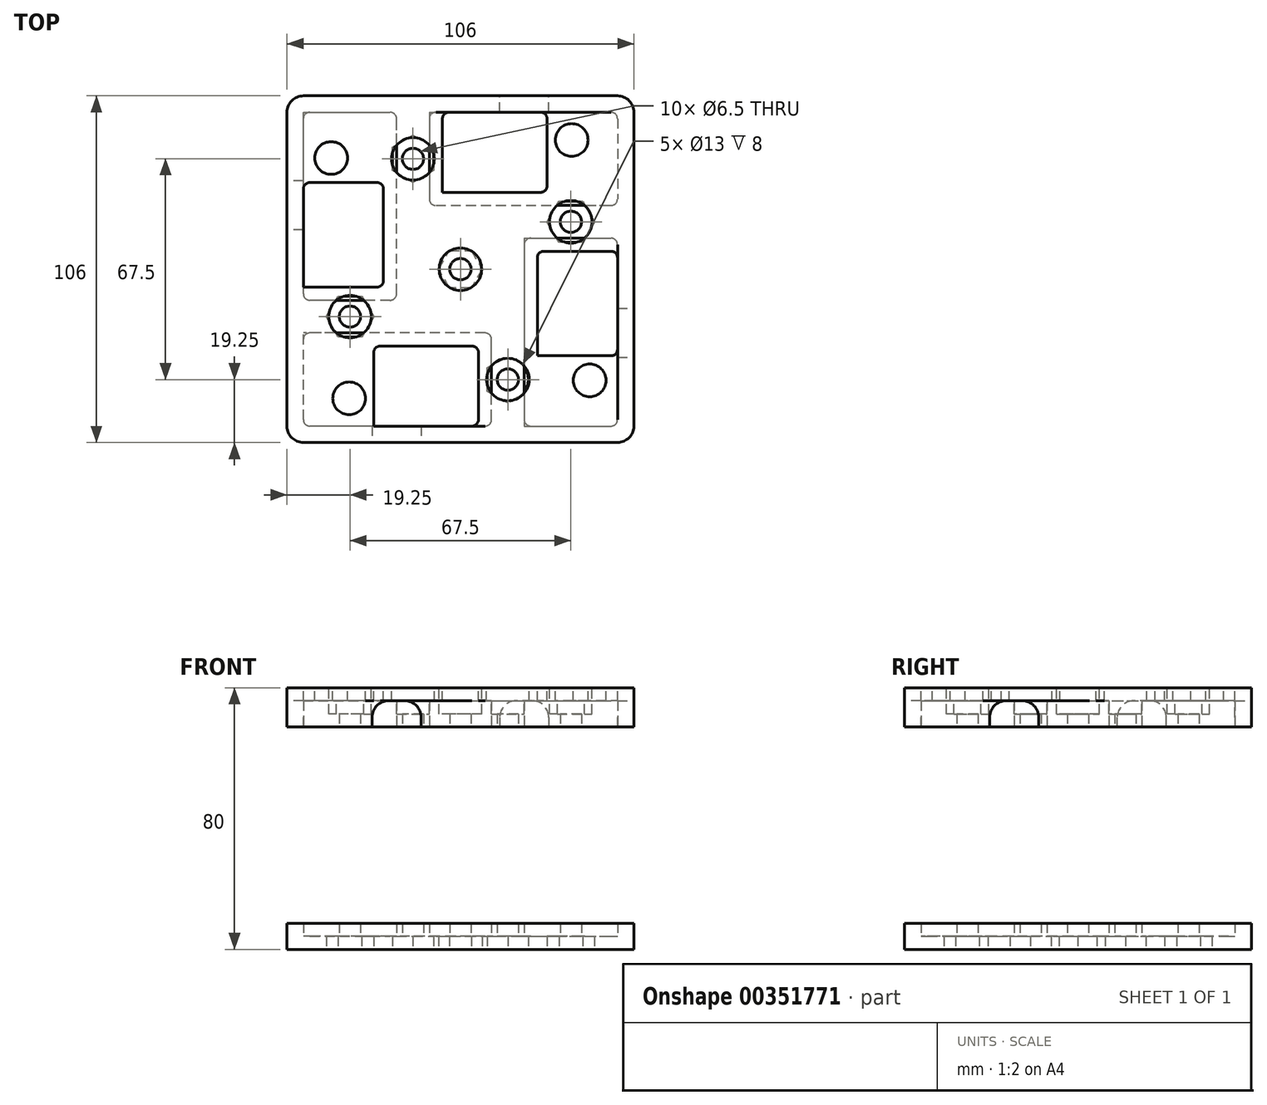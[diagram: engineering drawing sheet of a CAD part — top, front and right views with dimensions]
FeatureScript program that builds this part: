
annotation { "Feature Type Name" : "Feature", "Feature Type Description" : "" }
export const myFeature = defineFeature(function(context is Context, id is Id, definition is map)
    precondition{}
    {
        {
            var Q0;
            Q0=qCreatedBy(makeId("Top.planeOp"),FACE);
            var sketch = newSketch(context, id + "F0", { "sketchPlane" : qUnion([Q0])});
            skPoint(sketch, "E0.middle", {"position": v(0, 0) * mm});
            skCircle(sketch, "E1", {"center": v(0, 0) * mm, "radius": 3.25 * mm});
            skLineSegment(sketch, "E2.bottom", {"start": v(14.5, 14.5) * mm, "end": v(53, 14.5) * mm});
            skLineSegment(sketch, "E2.top", {"start": v(14.5, -53) * mm, "end": v(53, -53) * mm});
            skLineSegment(sketch, "E2.left", {"start": v(14.5, 14.5) * mm, "end": v(14.5, -53) * mm});
            skLineSegment(sketch, "E2.right", {"start": v(53, 14.5) * mm, "end": v(53, -53) * mm});
            skLineSegment(sketch, "E3.0", {"start": v(19.5, 9.5) * mm, "end": v(48, 9.5) * mm});
            skLineSegment(sketch, "E3.1", {"start": v(19.5, 9.5) * mm, "end": v(19.5, -48) * mm});
            skLineSegment(sketch, "E3.2", {"start": v(19.5, -48) * mm, "end": v(48, -48) * mm});
            skLineSegment(sketch, "E3.3", {"start": v(48, 9.5) * mm, "end": v(48, -48) * mm});
            skLineSegment(sketch, "E4.bottom", {"start": v(14.5, -53) * mm, "end": v(-53, -53) * mm});
            skLineSegment(sketch, "E4.top", {"start": v(14.5, -14.5) * mm, "end": v(-53, -14.5) * mm});
            skLineSegment(sketch, "E4.left", {"start": v(14.5, -53) * mm, "end": v(14.5, -14.5) * mm});
            skLineSegment(sketch, "E4.right", {"start": v(-53, -53) * mm, "end": v(-53, -14.5) * mm});
            skLineSegment(sketch, "E5.bottom", {"start": v(-53, -14.5) * mm, "end": v(-14.5, -14.5) * mm});
            skLineSegment(sketch, "E5.top", {"start": v(-53, 53) * mm, "end": v(-14.5, 53) * mm});
            skLineSegment(sketch, "E5.left", {"start": v(-53, -14.5) * mm, "end": v(-53, 53) * mm});
            skLineSegment(sketch, "E6.bottom", {"start": v(-14.5, 53) * mm, "end": v(53, 53) * mm});
            skLineSegment(sketch, "E6.right", {"start": v(53, 53) * mm, "end": v(53, 14.5) * mm});
            skLineSegment(sketch, "E7.0", {"start": v(-9.5, 19.5) * mm, "end": v(48, 19.5) * mm});
            skLineSegment(sketch, "E7.1", {"start": v(48, 48) * mm, "end": v(48, 19.5) * mm});
            skLineSegment(sketch, "E7.2", {"start": v(-9.5, 48) * mm, "end": v(48, 48) * mm});
            skLineSegment(sketch, "E8.0", {"start": v(-19.5, -9.5) * mm, "end": v(-19.5, 48) * mm});
            skLineSegment(sketch, "E8.1", {"start": v(-48, 48) * mm, "end": v(-19.5, 48) * mm});
            skLineSegment(sketch, "E9", {"start": v(-9.5, 48) * mm, "end": v(-9.5, 19.5) * mm});
            skLineSegment(sketch, "E10", {"start": v(-19.5, -9.5) * mm, "end": v(-48, -9.5) * mm});
            skLineSegment(sketch, "E11.trimOffspring", {"start": v(-48, -9.5) * mm, "end": v(-48, 48) * mm});
            skLineSegment(sketch, "E12.0", {"start": v(9.5, -19.5) * mm, "end": v(-48, -19.5) * mm});
            skLineSegment(sketch, "E12.1", {"start": v(9.5, -48) * mm, "end": v(9.5, -19.5) * mm});
            skLineSegment(sketch, "E12.2", {"start": v(9.5, -48) * mm, "end": v(-48, -48) * mm});
            skLineSegment(sketch, "E12.3", {"start": v(-48, -48) * mm, "end": v(-48, -19.5) * mm});
            skLineSegment(sketch, "E13", {"start": v(-14.5, 53) * mm, "end": v(-14.5, -14.5) * mm});
            skLineSegment(sketch, "E14", {"start": v(14.5, 14.5) * mm, "end": v(-14.5, 14.5) * mm});
            skCircle(sketch, "E15", {"center": v(14.5, -33.75) * mm, "radius": 3.25 * mm});
            skCircle(sketch, "E16", {"center": v(-33.75, -14.5) * mm, "radius": 3.25 * mm});
            skCircle(sketch, "E17", {"center": v(33.75, 14.5) * mm, "radius": 3.25 * mm});
            skCircle(sketch, "E18", {"center": v(-14.5, 33.75) * mm, "radius": 3.25 * mm});
            skPoint(sketch, "E19.0.midPoint", {"position": v(20.3, -33.75) * mm});
            skLineSegment(sketch, "E20.1.3", {"start": v(30.22, 19.5) * mm, "end": v(30.4, 19.81) * mm});
            skSolve(sketch);
        }
        {
            var Q0;
            Q0 = qSketchRegion(id + "F0", true);
            var Q1;
            Q1=makeQuery(id+"F0.imprint","IMPRINT",FACE,{"disambiguationData":[TD([[makeQuery(id+"F0.imprint","IMPRINT",EDGE,{"derivedFrom":sQuery(id+"F0.wireOp",EDGE,"E1")}),-1.0]])]});
            extrude(context, id + "F1", {"entities" : qUnion([Q0, Q1]), "depth" : 8 * mm, "offsetDistance" : 25 * mm});
        }
        {
            var Q0;
            Q0 = qSketchRegion(id + "F0", true);
            var Q1;
            Q1=makeQuery(id+"F0.imprint","IMPRINT",FACE,{"disambiguationData":[TD([[makeQuery(id+"F0.imprint","IMPRINT",EDGE,{"derivedFrom":sQuery(id+"F0.wireOp",EDGE,"E12.0")}),1.0]])]});
            var Q2;
            Q2=makeQuery(id+"F0.imprint","IMPRINT",FACE,{"disambiguationData":[TD([[makeQuery(id+"F0.imprint","IMPRINT",EDGE,{"derivedFrom":sQuery(id+"F0.wireOp",EDGE,"E8.0")}),1.0]])]});
            var Q3;
            {var subQ0=sQuery(id+"F0.wireOp",EDGE,"E7.1");Q3=makeQuery(id+"F0.imprint","IMPRINT",FACE,{"disambiguationData":[TD([[makeQuery(id+"F0.imprint","IMPRINT",EDGE,{"derivedFrom":subQ0}),-1.0]])]});}
            var Q4;
            Q4=makeQuery(id+"F0.imprint","IMPRINT",FACE,{"disambiguationData":[TD([[makeQuery(id+"F0.imprint","IMPRINT",EDGE,{"derivedFrom":sQuery(id+"F0.wireOp",EDGE,"E3.0")}),-1.0]])]});
            var Q5;
            Q5=makeQuery(id+"F0.imprint","IMPRINT",FACE,{"disambiguationData":[TD([[makeQuery(id+"F0.imprint","IMPRINT",EDGE,{"derivedFrom":sQuery(id+"F0.wireOp",EDGE,"E1")}),-1.0]])]});
            extrude(context, id + "F2", {"entities" : qUnion([Q0, Q1, Q2, Q3, Q4, Q5]), "operationType" : NewBodyOperationType.ADD, "depth" : 4 * mm, "offsetDistance" : 25 * mm});
        }
        {
            var Q0;
            Q0 = qSketchRegion(id + "F0", true);
            var Q1;
            Q1=makeQuery(id+"F0.imprint","IMPRINT",FACE,{"disambiguationData":[TD([[makeQuery(id+"F0.imprint","IMPRINT",EDGE,{"derivedFrom":sQuery(id+"F0.wireOp",EDGE,"E1")}),-1.0]])]});
            extrude(context, id + "F3", {"entities" : qUnion([Q0, Q1]), "depth" : 80 * mm, "offsetDistance" : 25 * mm, "hasSecondDirection" : true, "secondDirectionOppositeDirection" : false, "secondDirectionDepth" : 68 * mm});
        }
        {
            var Q0;
            Q0 = qSketchRegion(id + "F0", true);
            var Q1;
            Q1=makeQuery(id+"F2.boolean.opBoolean","SPLIT",FACE,{"disambiguationData":[TD([makeQuery(id+"F1.opExtrude","SWEPT_FACE",FACE,{"disambiguationData":[OSD([sQuery(id+"F0.wireOp",EDGE,"E8.0")])]})])],"derivedFrom":makeQuery(id+"F2.opExtrude","CAP_FACE",FACE,{"disambiguationData":[OSD([sQuery(id+"F0.wireOp",EDGE,"E1"),sQuery(id+"F0.wireOp",EDGE,"E2.top"),sQuery(id+"F0.wireOp",EDGE,"E2.right"),sQuery(id+"F0.wireOp",EDGE,"E4.bottom"),sQuery(id+"F0.wireOp",EDGE,"E4.right"),sQuery(id+"F0.wireOp",EDGE,"E5.top"),sQuery(id+"F0.wireOp",EDGE,"E5.left"),sQuery(id+"F0.wireOp",EDGE,"E6.bottom"),sQuery(id+"F0.wireOp",EDGE,"E6.right")])],"isStart":false})});
            var Q2;
            Q2=makeQuery(id+"F2.boolean.opBoolean","SPLIT",FACE,{"disambiguationData":[TD([makeQuery(id+"F1.opExtrude","SWEPT_FACE",FACE,{"disambiguationData":[OSD([sQuery(id+"F0.wireOp",EDGE,"E7.0")])]})])],"derivedFrom":makeQuery(id+"F2.opExtrude","CAP_FACE",FACE,{"disambiguationData":[OSD([sQuery(id+"F0.wireOp",EDGE,"E1"),sQuery(id+"F0.wireOp",EDGE,"E2.top"),sQuery(id+"F0.wireOp",EDGE,"E2.right"),sQuery(id+"F0.wireOp",EDGE,"E4.bottom"),sQuery(id+"F0.wireOp",EDGE,"E4.right"),sQuery(id+"F0.wireOp",EDGE,"E5.top"),sQuery(id+"F0.wireOp",EDGE,"E5.left"),sQuery(id+"F0.wireOp",EDGE,"E6.bottom"),sQuery(id+"F0.wireOp",EDGE,"E6.right")])],"isStart":false})});
            var Q3;
            Q3=makeQuery(id+"F2.boolean.opBoolean","SPLIT",FACE,{"disambiguationData":[TD([makeQuery(id+"F1.opExtrude","SWEPT_FACE",FACE,{"disambiguationData":[OSD([sQuery(id+"F0.wireOp",EDGE,"E3.0")])]})])],"derivedFrom":makeQuery(id+"F2.opExtrude","CAP_FACE",FACE,{"disambiguationData":[OSD([sQuery(id+"F0.wireOp",EDGE,"E1"),sQuery(id+"F0.wireOp",EDGE,"E2.top"),sQuery(id+"F0.wireOp",EDGE,"E2.right"),sQuery(id+"F0.wireOp",EDGE,"E4.bottom"),sQuery(id+"F0.wireOp",EDGE,"E4.right"),sQuery(id+"F0.wireOp",EDGE,"E5.top"),sQuery(id+"F0.wireOp",EDGE,"E5.left"),sQuery(id+"F0.wireOp",EDGE,"E6.bottom"),sQuery(id+"F0.wireOp",EDGE,"E6.right")])],"isStart":false})});
            var Q4;
            Q4=makeQuery(id+"F2.boolean.opBoolean","SPLIT",FACE,{"disambiguationData":[TD([makeQuery(id+"F1.opExtrude","SWEPT_FACE",FACE,{"disambiguationData":[OSD([sQuery(id+"F0.wireOp",EDGE,"E12.0")])]})])],"derivedFrom":makeQuery(id+"F2.opExtrude","CAP_FACE",FACE,{"disambiguationData":[OSD([sQuery(id+"F0.wireOp",EDGE,"E1"),sQuery(id+"F0.wireOp",EDGE,"E2.top"),sQuery(id+"F0.wireOp",EDGE,"E2.right"),sQuery(id+"F0.wireOp",EDGE,"E4.bottom"),sQuery(id+"F0.wireOp",EDGE,"E4.right"),sQuery(id+"F0.wireOp",EDGE,"E5.top"),sQuery(id+"F0.wireOp",EDGE,"E5.left"),sQuery(id+"F0.wireOp",EDGE,"E6.bottom"),sQuery(id+"F0.wireOp",EDGE,"E6.right")])],"isStart":false})});
            var Q5;
            {var subQ0=sQuery(id+"F0.wireOp",EDGE,"E1");Q5=makeQuery(id+"F2.boolean.opBoolean","SPLIT",FACE,{"disambiguationData":[TD([makeQuery(id+"F1.opExtrude","SWEPT_FACE",FACE,{"disambiguationData":[OSD([sQuery(id+"F0.wireOp",EDGE,"E2.left")])]})])],"derivedFrom":makeQuery(id+"F2.opExtrude","CAP_FACE",FACE,{"disambiguationData":[OSD([subQ0,sQuery(id+"F0.wireOp",EDGE,"E2.top"),sQuery(id+"F0.wireOp",EDGE,"E2.right"),sQuery(id+"F0.wireOp",EDGE,"E4.bottom"),sQuery(id+"F0.wireOp",EDGE,"E4.right"),sQuery(id+"F0.wireOp",EDGE,"E5.top"),sQuery(id+"F0.wireOp",EDGE,"E5.left"),sQuery(id+"F0.wireOp",EDGE,"E6.bottom"),sQuery(id+"F0.wireOp",EDGE,"E6.right")])],"isStart":false})});}
            extrude(context, id + "F4", {"entities" : qUnion([Q0, Q1, Q2, Q3, Q4, Q5]), "operationType" : NewBodyOperationType.ADD, "depth" : 76 * mm, "offsetDistance" : 25 * mm, "hasSecondDirection" : true, "secondDirectionOppositeDirection" : false, "secondDirectionDepth" : 72 * mm});
        }
        {
            var Q0;
            {var subQ0=sQuery(id+"F0.wireOp",EDGE,"E14");var subQ1=sQuery(id+"F0.wireOp",EDGE,"E2.left");var subQ2=sQuery(id+"F0.wireOp",EDGE,"E13");var subQ3=sQuery(id+"F0.wireOp",EDGE,"E4.top");var subQ4=sQuery(id+"F0.wireOp",EDGE,"E1");var subQ5=sQuery(id+"F0.wireOp",EDGE,"E6.right");var subQ6=sQuery(id+"F0.wireOp",EDGE,"E6.bottom");var subQ7=sQuery(id+"F0.wireOp",EDGE,"E5.left");var subQ8=sQuery(id+"F0.wireOp",EDGE,"E5.top");var subQ9=sQuery(id+"F0.wireOp",EDGE,"E4.right");var subQ10=sQuery(id+"F0.wireOp",EDGE,"E4.bottom");var subQ11=sQuery(id+"F0.wireOp",EDGE,"E2.right");var subQ12=sQuery(id+"F0.wireOp",EDGE,"E2.top");var subQ13=makeQuery(id+"F2.opExtrude","CAP_FACE",FACE,{"disambiguationData":[OSD([subQ4,subQ12,subQ11,subQ10,subQ9,subQ8,subQ7,subQ6,subQ5])],"isStart":false});var subQ14=sQuery(id+"F0.wireOp",EDGE,"E12.0");var subQ15=sQuery(id+"F0.wireOp",EDGE,"E12.1");var subQ16=sQuery(id+"F0.wireOp",EDGE,"E12.2");var subQ17=sQuery(id+"F0.wireOp",EDGE,"E12.3");var subQ18=sQuery(id+"F0.wireOp",EDGE,"E8.0");var subQ19=sQuery(id+"F0.wireOp",EDGE,"E8.1");var subQ20=sQuery(id+"F0.wireOp",EDGE,"E10");var subQ21=sQuery(id+"F0.wireOp",EDGE,"E11.trimOffspring");var subQ22=sQuery(id+"F0.wireOp",EDGE,"E7.0");var subQ23=sQuery(id+"F0.wireOp",EDGE,"E9");var subQ24=sQuery(id+"F0.wireOp",EDGE,"E7.1");var subQ25=sQuery(id+"F0.wireOp",EDGE,"E7.2");var subQ26=sQuery(id+"F0.wireOp",EDGE,"E3.0");var subQ27=sQuery(id+"F0.wireOp",EDGE,"E3.1");var subQ28=sQuery(id+"F0.wireOp",EDGE,"E3.2");var subQ29=sQuery(id+"F0.wireOp",EDGE,"E3.3");Q0=makeQuery(id+"F4.boolean.opBoolean","MERGE",FACE,{"derivedFrom":[makeQuery(id+"F3.opExtrude","CAP_FACE",FACE,{"disambiguationData":[OSD([subQ12,subQ1,subQ11,subQ26,subQ27,subQ28,subQ29,subQ10,subQ3,subQ9,subQ8,subQ7,subQ6,subQ5,subQ22,subQ24,subQ25,subQ18,subQ19,subQ23,subQ20,subQ21,subQ14,subQ15,subQ16,subQ17,subQ2,subQ0])],"isStart":false}),makeQuery(id+"F4.opExtrude","CAP_FACE",FACE,{"disambiguationData":[OSD([subQ4,subQ12,subQ11,subQ10,subQ9,subQ8,subQ7,subQ6,subQ5]),TDD([makeQuery(id+"F2.boolean.opBoolean","SPLIT",FACE,{"disambiguationData":[TD([makeQuery(id+"F1.opExtrude","SWEPT_FACE",FACE,{"disambiguationData":[OSD([subQ26])]})])],"derivedFrom":subQ13})])],"isStart":false}),makeQuery(id+"F4.opExtrude","CAP_FACE",FACE,{"disambiguationData":[OSD([subQ4,subQ12,subQ11,subQ10,subQ9,subQ8,subQ7,subQ6,subQ5]),TDD([makeQuery(id+"F2.boolean.opBoolean","SPLIT",FACE,{"disambiguationData":[TD([makeQuery(id+"F1.opExtrude","SWEPT_FACE",FACE,{"disambiguationData":[OSD([subQ22])]})])],"derivedFrom":subQ13})])],"isStart":false}),makeQuery(id+"F4.opExtrude","CAP_FACE",FACE,{"disambiguationData":[OSD([subQ4,subQ12,subQ11,subQ10,subQ9,subQ8,subQ7,subQ6,subQ5]),TDD([makeQuery(id+"F2.boolean.opBoolean","SPLIT",FACE,{"disambiguationData":[TD([makeQuery(id+"F1.opExtrude","SWEPT_FACE",FACE,{"disambiguationData":[OSD([subQ18])]})])],"derivedFrom":subQ13})])],"isStart":false}),makeQuery(id+"F4.opExtrude","CAP_FACE",FACE,{"disambiguationData":[OSD([subQ4,subQ12,subQ11,subQ10,subQ9,subQ8,subQ7,subQ6,subQ5]),TDD([makeQuery(id+"F2.boolean.opBoolean","SPLIT",FACE,{"disambiguationData":[TD([makeQuery(id+"F1.opExtrude","SWEPT_FACE",FACE,{"disambiguationData":[OSD([subQ14])]})])],"derivedFrom":subQ13})])],"isStart":false}),makeQuery(id+"F4.opExtrude","CAP_FACE",FACE,{"disambiguationData":[OSD([subQ4,subQ12,subQ11,subQ10,subQ9,subQ8,subQ7,subQ6,subQ5]),TDD([makeQuery(id+"F2.boolean.opBoolean","SPLIT",FACE,{"disambiguationData":[TD([makeQuery(id+"F1.opExtrude","SWEPT_FACE",FACE,{"disambiguationData":[OSD([subQ1])]})])],"derivedFrom":subQ13})])],"isStart":false})]});}
            var sketch = newSketch(context, id + "F5", { "sketchPlane" : qUnion([Q0])});
            skLineSegment(sketch, "E21.bottom", {"start": v(23.5, 5.5) * mm, "end": v(48, 5.5) * mm});
            skLineSegment(sketch, "E21.top", {"start": v(23.5, -26.5) * mm, "end": v(48, -26.5) * mm});
            skLineSegment(sketch, "E21.left", {"start": v(23.5, 5.5) * mm, "end": v(23.5, -26.5) * mm});
            skLineSegment(sketch, "E21.right", {"start": v(48, 5.5) * mm, "end": v(48, -26.5) * mm});
            skCircle(sketch, "E22", {"center": v(39.5, -34) * mm, "radius": 5 * mm});
            skPoint(sketch, "E23.center", {"position": v(0, 0) * mm});
            skCircle(sketch, "E24", {"center": v(0, 0) * mm, "radius": 9 * mm, "construction": true});
            skLineSegment(sketch, "E25.1.0", {"start": v(-5.5, 48) * mm, "end": v(26.5, 48) * mm});
            skLineSegment(sketch, "E25.1.1", {"start": v(-5.5, 23.5) * mm, "end": v(-5.5, 48) * mm});
            skLineSegment(sketch, "E25.1.2", {"start": v(-5.5, 23.5) * mm, "end": v(26.5, 23.5) * mm});
            skLineSegment(sketch, "E25.1.3", {"start": v(26.5, 23.5) * mm, "end": v(26.5, 48) * mm});
            skCircle(sketch, "E25.1.4", {"center": v(34, 39.5) * mm, "radius": 5 * mm});
            skLineSegment(sketch, "E25.2.0", {"start": v(-48, -5.5) * mm, "end": v(-48, 26.5) * mm});
            skLineSegment(sketch, "E25.2.1", {"start": v(-23.5, -5.5) * mm, "end": v(-48, -5.5) * mm});
            skLineSegment(sketch, "E25.2.2", {"start": v(-23.5, -5.5) * mm, "end": v(-23.5, 26.5) * mm});
            skLineSegment(sketch, "E25.2.3", {"start": v(-23.5, 26.5) * mm, "end": v(-48, 26.5) * mm});
            skCircle(sketch, "E25.2.4", {"center": v(-39.5, 34) * mm, "radius": 5 * mm});
            skLineSegment(sketch, "E25.3.0", {"start": v(5.5, -48) * mm, "end": v(-26.5, -48) * mm});
            skLineSegment(sketch, "E25.3.1", {"start": v(5.5, -23.5) * mm, "end": v(5.5, -48) * mm});
            skLineSegment(sketch, "E25.3.2", {"start": v(5.5, -23.5) * mm, "end": v(-26.5, -23.5) * mm});
            skLineSegment(sketch, "E25.3.3", {"start": v(-26.5, -23.5) * mm, "end": v(-26.5, -48) * mm});
            skCircle(sketch, "E25.3.4", {"center": v(-34, -39.5) * mm, "radius": 5 * mm});
            skSolve(sketch);
        }
        {
            var Q0;
            Q0 = qSketchRegion(id + "F5", true);
            extrude(context, id + "F6", {"entities" : qUnion([Q0]), "operationType" : NewBodyOperationType.REMOVE, "oppositeDirection" : true, "depth" : 25 * mm, "offsetDistance" : 25 * mm});
        }
        {
            var Q0;
            Q0=makeQuery(id+"F3.opExtrude","SWEPT_FACE",FACE,{"disambiguationData":[OSD([sQuery(id+"F0.wireOp",EDGE,"E2.right"),sQuery(id+"F0.wireOp",EDGE,"E6.right")])]});
            var sketch = newSketch(context, id + "F7", { "sketchPlane" : qUnion([Q0])});
            skLineSegment(sketch, "E26.top", {"start": v(-27, 76) * mm, "end": v(-12, 76) * mm});
            skLineSegment(sketch, "E26.left", {"start": v(-27, 68) * mm, "end": v(-27, 76) * mm});
            skLineSegment(sketch, "E26.right", {"start": v(-12, 72) * mm, "end": v(-12, 76) * mm});
            skLineSegment(sketch, "E27", {"start": v(-12, 76) * mm, "end": v(-12, 68) * mm});
            skSolve(sketch);
        }
        {
            var Q0;
            Q0=makeQuery(id+"F3.opExtrude","SWEPT_FACE",FACE,{"disambiguationData":[OSD([sQuery(id+"F0.wireOp",EDGE,"E5.top"),sQuery(id+"F0.wireOp",EDGE,"E6.bottom")])]});
            var sketch = newSketch(context, id + "F8", { "sketchPlane" : qUnion([Q0])});
            skLineSegment(sketch, "E28.bottom", {"start": v(-27, 76) * mm, "end": v(-12, 76) * mm});
            skLineSegment(sketch, "E28.top", {"start": v(-27, 68) * mm, "end": v(-12, 68) * mm});
            skLineSegment(sketch, "E28.left", {"start": v(-27, 76) * mm, "end": v(-27, 68) * mm});
            skLineSegment(sketch, "E28.right", {"start": v(-12, 76) * mm, "end": v(-12, 68) * mm});
            skSolve(sketch);
        }
        {
            var Q0;
            Q0=makeQuery(id+"F3.opExtrude","SWEPT_FACE",FACE,{"disambiguationData":[OSD([sQuery(id+"F0.wireOp",EDGE,"E4.right"),sQuery(id+"F0.wireOp",EDGE,"E5.left")])]});
            var sketch = newSketch(context, id + "F9", { "sketchPlane" : qUnion([Q0])});
            skLineSegment(sketch, "E29.bottom", {"start": v(-27, 68) * mm, "end": v(-12, 68) * mm});
            skLineSegment(sketch, "E29.top", {"start": v(-27, 76) * mm, "end": v(-12, 76) * mm});
            skLineSegment(sketch, "E29.left", {"start": v(-27, 68) * mm, "end": v(-27, 76) * mm});
            skLineSegment(sketch, "E29.right", {"start": v(-12, 68) * mm, "end": v(-12, 76) * mm});
            skSolve(sketch);
        }
        {
            var Q0;
            Q0=makeQuery(id+"F3.opExtrude","SWEPT_FACE",FACE,{"disambiguationData":[OSD([sQuery(id+"F0.wireOp",EDGE,"E2.top"),sQuery(id+"F0.wireOp",EDGE,"E4.bottom")])]});
            var sketch = newSketch(context, id + "F10", { "sketchPlane" : qUnion([Q0])});
            skLineSegment(sketch, "E30.bottom", {"start": v(-27, 68) * mm, "end": v(-12, 68) * mm});
            skLineSegment(sketch, "E30.top", {"start": v(-27, 76) * mm, "end": v(-12, 76) * mm});
            skLineSegment(sketch, "E30.left", {"start": v(-27, 68) * mm, "end": v(-27, 76) * mm});
            skLineSegment(sketch, "E30.right", {"start": v(-12, 68) * mm, "end": v(-12, 76) * mm});
            skSolve(sketch);
        }
        {
            var Q0;
            Q0=makeQuery(id+"F8.imprint","IMPRINT",FACE,{"disambiguationData":[TD([[makeQuery(id+"F8.imprint","IMPRINT",EDGE,{"derivedFrom":sQuery(id+"F8.wireOp",EDGE,"E28.bottom")}),-1.0]])]});
            extrude(context, id + "F11", {"entities" : qUnion([Q0]), "operationType" : NewBodyOperationType.REMOVE, "oppositeDirection" : true, "depth" : 5 * mm, "offsetDistance" : 25 * mm});
        }
        {
            var Q0;
            Q0=makeQuery(id+"F9.imprint","IMPRINT",FACE,{"disambiguationData":[TD([[makeQuery(id+"F9.imprint","IMPRINT",EDGE,{"derivedFrom":sQuery(id+"F9.wireOp",EDGE,"E29.bottom")}),-1.0]])]});
            extrude(context, id + "F12", {"entities" : qUnion([Q0]), "operationType" : NewBodyOperationType.REMOVE, "oppositeDirection" : true, "depth" : 5 * mm, "offsetDistance" : 25 * mm});
        }
        {
            var Q0;
            Q0=makeQuery(id+"F10.imprint","IMPRINT",FACE,{"disambiguationData":[TD([[makeQuery(id+"F10.imprint","IMPRINT",EDGE,{"derivedFrom":sQuery(id+"F10.wireOp",EDGE,"E30.bottom")}),1.0]])]});
            extrude(context, id + "F13", {"entities" : qUnion([Q0]), "operationType" : NewBodyOperationType.REMOVE, "oppositeDirection" : true, "depth" : 5 * mm, "offsetDistance" : 25 * mm});
        }
        {
            var Q0;
            Q0=makeQuery(id+"F7.imprint","IMPRINT",FACE,{"disambiguationData":[TD([[makeQuery(id+"F7.imprint","IMPRINT",EDGE,{"derivedFrom":sQuery(id+"F7.wireOp",EDGE,"E26.top")}),-1.0]])]});
            extrude(context, id + "F14", {"entities" : qUnion([Q0]), "operationType" : NewBodyOperationType.REMOVE, "oppositeDirection" : true, "depth" : 5 * mm, "offsetDistance" : 25 * mm});
        }
        {
            var Q0;
            Q0=makeQuery(id+"F14.boolean.opBoolean","COPY",EDGE,{"derivedFrom":makeQuery(id+"F14.opExtrude","SWEPT_EDGE",EDGE,{"disambiguationData":[OSD([sQuery(id+"F7.wireOp",EDGE,"E26.top"),sQuery(id+"F7.wireOp",EDGE,"E26.right")])]})});
            var Q1;
            Q1=makeQuery(id+"F14.boolean.opBoolean","COPY",EDGE,{"derivedFrom":makeQuery(id+"F14.opExtrude","SWEPT_EDGE",EDGE,{"disambiguationData":[OSD([sQuery(id+"F7.wireOp",EDGE,"E26.top"),sQuery(id+"F7.wireOp",EDGE,"E26.left")])]})});
            var Q2;
            Q2=makeQuery(id+"F11.boolean.opBoolean","COPY",EDGE,{"derivedFrom":makeQuery(id+"F11.opExtrude","SWEPT_EDGE",EDGE,{"disambiguationData":[OSD([sQuery(id+"F8.wireOp",EDGE,"E28.bottom"),sQuery(id+"F8.wireOp",EDGE,"E28.left")])]})});
            var Q3;
            Q3=makeQuery(id+"F13.boolean.opBoolean","COPY",EDGE,{"derivedFrom":makeQuery(id+"F13.opExtrude","SWEPT_EDGE",EDGE,{"disambiguationData":[OSD([sQuery(id+"F10.wireOp",EDGE,"E30.top"),sQuery(id+"F10.wireOp",EDGE,"E30.right")])]})});
            var Q4;
            Q4=makeQuery(id+"F13.boolean.opBoolean","COPY",EDGE,{"derivedFrom":makeQuery(id+"F13.opExtrude","SWEPT_EDGE",EDGE,{"disambiguationData":[OSD([sQuery(id+"F10.wireOp",EDGE,"E30.top"),sQuery(id+"F10.wireOp",EDGE,"E30.left")])]})});
            var Q5;
            Q5=makeQuery(id+"F11.boolean.opBoolean","COPY",EDGE,{"derivedFrom":makeQuery(id+"F11.opExtrude","SWEPT_EDGE",EDGE,{"disambiguationData":[OSD([sQuery(id+"F8.wireOp",EDGE,"E28.bottom"),sQuery(id+"F8.wireOp",EDGE,"E28.right")])]})});
            var Q6;
            Q6=makeQuery(id+"F12.boolean.opBoolean","COPY",EDGE,{"derivedFrom":makeQuery(id+"F12.opExtrude","SWEPT_EDGE",EDGE,{"disambiguationData":[OSD([sQuery(id+"F9.wireOp",EDGE,"E29.top"),sQuery(id+"F9.wireOp",EDGE,"E29.left")])]})});
            var Q7;
            Q7=makeQuery(id+"F12.boolean.opBoolean","COPY",EDGE,{"derivedFrom":makeQuery(id+"F12.opExtrude","SWEPT_EDGE",EDGE,{"disambiguationData":[OSD([sQuery(id+"F9.wireOp",EDGE,"E29.top"),sQuery(id+"F9.wireOp",EDGE,"E29.right")])]})});
            var Q8;
            Q8=makeQuery(id+"F3.opExtrude","SWEPT_EDGE",EDGE,{"disambiguationData":[OSD([sQuery(id+"F0.wireOp",EDGE,"qEaCc7V0-lVzf-c6JI-c2TC-OOMBXQbIOkhG.top"),sQuery(id+"F0.wireOp",EDGE,"qEaCc7V0-lVzf-c6JI-c2TC-OOMBXQbIOkhG.right")])]});
            var Q9;
            Q9=makeQuery(id+"F3.opExtrude","SWEPT_EDGE",EDGE,{"disambiguationData":[OSD([sQuery(id+"F0.wireOp",EDGE,"cmqrVWR0-jSFe-Savq-fu5a-hjZHoR7EivpK.top"),sQuery(id+"F0.wireOp",EDGE,"cmqrVWR0-jSFe-Savq-fu5a-hjZHoR7EivpK.right")])]});
            var Q10;
            Q10=makeQuery(id+"F3.opExtrude","SWEPT_EDGE",EDGE,{"disambiguationData":[OSD([sQuery(id+"F0.wireOp",EDGE,"iMNMKOWt-2Doy-GwoA-sGvh-06eOiazu1pcB.top"),sQuery(id+"F0.wireOp",EDGE,"iMNMKOWt-2Doy-GwoA-sGvh-06eOiazu1pcB.left")])]});
            var Q11;
            Q11=makeQuery(id+"F3.opExtrude","SWEPT_EDGE",EDGE,{"disambiguationData":[OSD([sQuery(id+"F0.wireOp",EDGE,"4UJuQncx-ghhf-1D9n-JMAU-exmbqmwtyDKx.top"),sQuery(id+"F0.wireOp",EDGE,"4UJuQncx-ghhf-1D9n-JMAU-exmbqmwtyDKx.right")])]});
            var Q12;
            Q12=makeQuery(id+"F3.opExtrude","SWEPT_EDGE",EDGE,{"disambiguationData":[OSD([sQuery(id+"F0.wireOp",EDGE,"E5.top"),sQuery(id+"F0.wireOp",EDGE,"E5.left")])]});
            var Q13;
            Q13=makeQuery(id+"F3.opExtrude","SWEPT_EDGE",EDGE,{"disambiguationData":[OSD([sQuery(id+"F0.wireOp",EDGE,"E6.bottom"),sQuery(id+"F0.wireOp",EDGE,"E6.right")])]});
            var Q14;
            Q14=makeQuery(id+"F3.opExtrude","SWEPT_EDGE",EDGE,{"disambiguationData":[OSD([sQuery(id+"F0.wireOp",EDGE,"E2.top"),sQuery(id+"F0.wireOp",EDGE,"E2.right")])]});
            var Q15;
            Q15=makeQuery(id+"F3.opExtrude","SWEPT_EDGE",EDGE,{"disambiguationData":[OSD([sQuery(id+"F0.wireOp",EDGE,"E4.bottom"),sQuery(id+"F0.wireOp",EDGE,"E4.right")])]});
            var Q16;
            Q16=makeQuery(id+"F1.opExtrude","SWEPT_EDGE",EDGE,{"disambiguationData":[OSD([sQuery(id+"F0.wireOp",EDGE,"E4.bottom"),sQuery(id+"F0.wireOp",EDGE,"E4.right")])]});
            var Q17;
            Q17=makeQuery(id+"F1.opExtrude","SWEPT_EDGE",EDGE,{"disambiguationData":[OSD([sQuery(id+"F0.wireOp",EDGE,"E5.top"),sQuery(id+"F0.wireOp",EDGE,"E5.left")])]});
            var Q18;
            Q18=makeQuery(id+"F1.opExtrude","SWEPT_EDGE",EDGE,{"disambiguationData":[OSD([sQuery(id+"F0.wireOp",EDGE,"E6.bottom"),sQuery(id+"F0.wireOp",EDGE,"E6.right")])]});
            var Q19;
            Q19=makeQuery(id+"F1.opExtrude","SWEPT_EDGE",EDGE,{"disambiguationData":[OSD([sQuery(id+"F0.wireOp",EDGE,"E2.top"),sQuery(id+"F0.wireOp",EDGE,"E2.right")])]});
            fillet(context, id + "F15", {"entities" : qUnion([Q0, Q1, Q2, Q3, Q4, Q5, Q6, Q7, Q8, Q9, Q10, Q11, Q12, Q13, Q14, Q15, Q16, Q17, Q18, Q19]), "radius" : 5 * mm, "tangentPropagation" : true, "allowEdgeOverflow" : false});
        }
        {
            var Q0;
            Q0=makeQuery(id+"F6.boolean.opBoolean","COPY",EDGE,{"derivedFrom":makeQuery(id+"F6.opExtrude","SWEPT_EDGE",EDGE,{"disambiguationData":[OSD([sQuery(id+"F5.wireOp",EDGE,"E25.2.0"),sQuery(id+"F5.wireOp",EDGE,"E25.2.3")])]})});
            var Q1;
            Q1=makeQuery(id+"F6.boolean.opBoolean","COPY",EDGE,{"derivedFrom":makeQuery(id+"F6.opExtrude","SWEPT_EDGE",EDGE,{"disambiguationData":[OSD([sQuery(id+"F5.wireOp",EDGE,"E25.1.0"),sQuery(id+"F5.wireOp",EDGE,"E25.1.1")])]})});
            var Q2;
            Q2=makeQuery(id+"F6.boolean.opBoolean","COPY",EDGE,{"derivedFrom":makeQuery(id+"F6.opExtrude","SWEPT_EDGE",EDGE,{"disambiguationData":[OSD([sQuery(id+"F5.wireOp",EDGE,"E21.bottom"),sQuery(id+"F5.wireOp",EDGE,"E21.left")])]})});
            var Q3;
            Q3=makeQuery(id+"F6.boolean.opBoolean","COPY",EDGE,{"derivedFrom":makeQuery(id+"F6.opExtrude","SWEPT_EDGE",EDGE,{"disambiguationData":[OSD([sQuery(id+"F5.wireOp",EDGE,"E25.3.2"),sQuery(id+"F5.wireOp",EDGE,"E25.3.3")])]})});
            var Q4;
            Q4=makeQuery(id+"F6.boolean.opBoolean","COPY",EDGE,{"derivedFrom":makeQuery(id+"F6.opExtrude","SWEPT_EDGE",EDGE,{"disambiguationData":[OSD([sQuery(id+"F5.wireOp",EDGE,"E25.1.0"),sQuery(id+"F5.wireOp",EDGE,"E25.1.3")])]})});
            var Q5;
            Q5=makeQuery(id+"F6.boolean.opBoolean","COPY",EDGE,{"derivedFrom":makeQuery(id+"F6.opExtrude","SWEPT_EDGE",EDGE,{"disambiguationData":[OSD([sQuery(id+"F5.wireOp",EDGE,"E25.2.2"),sQuery(id+"F5.wireOp",EDGE,"E25.2.3")])]})});
            var Q6;
            Q6=makeQuery(id+"F6.boolean.opBoolean","COPY",EDGE,{"derivedFrom":makeQuery(id+"F6.opExtrude","SWEPT_EDGE",EDGE,{"disambiguationData":[OSD([sQuery(id+"F5.wireOp",EDGE,"E25.3.1"),sQuery(id+"F5.wireOp",EDGE,"E25.3.2")])]})});
            var Q7;
            Q7=makeQuery(id+"F6.boolean.opBoolean","COPY",EDGE,{"derivedFrom":makeQuery(id+"F6.opExtrude","SWEPT_EDGE",EDGE,{"disambiguationData":[OSD([sQuery(id+"F5.wireOp",EDGE,"E21.bottom"),sQuery(id+"F5.wireOp",EDGE,"E21.right")])]})});
            var Q8;
            Q8=makeQuery(id+"F6.boolean.opBoolean","COPY",EDGE,{"derivedFrom":makeQuery(id+"F6.opExtrude","SWEPT_EDGE",EDGE,{"disambiguationData":[OSD([sQuery(id+"F5.wireOp",EDGE,"E25.1.2"),sQuery(id+"F5.wireOp",EDGE,"E25.1.3")])]})});
            var Q9;
            Q9=makeQuery(id+"F6.boolean.opBoolean","COPY",EDGE,{"derivedFrom":makeQuery(id+"F6.opExtrude","SWEPT_EDGE",EDGE,{"disambiguationData":[OSD([sQuery(id+"F5.wireOp",EDGE,"E21.top"),sQuery(id+"F5.wireOp",EDGE,"E21.right")])]})});
            var Q10;
            Q10=makeQuery(id+"F6.boolean.opBoolean","COPY",EDGE,{"derivedFrom":makeQuery(id+"F6.opExtrude","SWEPT_EDGE",EDGE,{"disambiguationData":[OSD([sQuery(id+"F5.wireOp",EDGE,"E25.3.0"),sQuery(id+"F5.wireOp",EDGE,"E25.3.1")])]})});
            var Q11;
            Q11=makeQuery(id+"F6.boolean.opBoolean","COPY",EDGE,{"derivedFrom":makeQuery(id+"F6.opExtrude","SWEPT_EDGE",EDGE,{"disambiguationData":[OSD([sQuery(id+"F5.wireOp",EDGE,"E25.2.1"),sQuery(id+"F5.wireOp",EDGE,"E25.2.2")])]})});
            var Q12;
            Q12=makeQuery(id+"F3.opExtrude","SWEPT_EDGE",EDGE,{"disambiguationData":[OSD([sQuery(id+"F0.wireOp",EDGE,"E12.2"),sQuery(id+"F0.wireOp",EDGE,"E12.3")])]});
            var Q13;
            Q13=makeQuery(id+"F3.opExtrude","SWEPT_EDGE",EDGE,{"disambiguationData":[OSD([sQuery(id+"F0.wireOp",EDGE,"E10"),sQuery(id+"F0.wireOp",EDGE,"E11.trimOffspring")])]});
            var Q14;
            Q14=makeQuery(id+"F3.opExtrude","SWEPT_EDGE",EDGE,{"disambiguationData":[OSD([sQuery(id+"F0.wireOp",EDGE,"E7.0"),sQuery(id+"F0.wireOp",EDGE,"E9")])]});
            var Q15;
            Q15=makeQuery(id+"F3.opExtrude","SWEPT_EDGE",EDGE,{"disambiguationData":[OSD([sQuery(id+"F0.wireOp",EDGE,"E3.1"),sQuery(id+"F0.wireOp",EDGE,"E3.2")])]});
            var Q16;
            Q16=makeQuery(id+"F3.opExtrude","SWEPT_EDGE",EDGE,{"disambiguationData":[OSD([sQuery(id+"F0.wireOp",EDGE,"E7.0"),sQuery(id+"F0.wireOp",EDGE,"E7.1")])]});
            var Q17;
            Q17=makeQuery(id+"F3.opExtrude","SWEPT_EDGE",EDGE,{"disambiguationData":[OSD([sQuery(id+"F0.wireOp",EDGE,"E3.2"),sQuery(id+"F0.wireOp",EDGE,"E3.3")])]});
            var Q18;
            Q18=makeQuery(id+"F3.opExtrude","SWEPT_EDGE",EDGE,{"disambiguationData":[OSD([sQuery(id+"F0.wireOp",EDGE,"E8.0"),sQuery(id+"F0.wireOp",EDGE,"E10")])]});
            var Q19;
            Q19=makeQuery(id+"F3.opExtrude","SWEPT_EDGE",EDGE,{"disambiguationData":[OSD([sQuery(id+"F0.wireOp",EDGE,"E12.1"),sQuery(id+"F0.wireOp",EDGE,"E12.2")])]});
            var Q20;
            Q20=makeQuery(id+"F3.opExtrude","SWEPT_EDGE",EDGE,{"disambiguationData":[OSD([sQuery(id+"F0.wireOp",EDGE,"E3.0"),sQuery(id+"F0.wireOp",EDGE,"E3.3")])]});
            var Q21;
            Q21=makeQuery(id+"F3.opExtrude","SWEPT_EDGE",EDGE,{"disambiguationData":[OSD([sQuery(id+"F0.wireOp",EDGE,"E7.1"),sQuery(id+"F0.wireOp",EDGE,"E7.2")])]});
            var Q22;
            Q22=makeQuery(id+"F3.opExtrude","SWEPT_EDGE",EDGE,{"disambiguationData":[OSD([sQuery(id+"F0.wireOp",EDGE,"E8.0"),sQuery(id+"F0.wireOp",EDGE,"E8.1")])]});
            var Q23;
            Q23=makeQuery(id+"F3.opExtrude","SWEPT_EDGE",EDGE,{"disambiguationData":[OSD([sQuery(id+"F0.wireOp",EDGE,"E12.0"),sQuery(id+"F0.wireOp",EDGE,"E12.1")])]});
            var Q24;
            Q24=makeQuery(id+"F1.opExtrude","SWEPT_EDGE",EDGE,{"disambiguationData":[OSD([sQuery(id+"F0.wireOp",EDGE,"E3.2"),sQuery(id+"F0.wireOp",EDGE,"E3.3")])]});
            var Q25;
            Q25=makeQuery(id+"F1.opExtrude","SWEPT_EDGE",EDGE,{"disambiguationData":[OSD([sQuery(id+"F0.wireOp",EDGE,"E12.1"),sQuery(id+"F0.wireOp",EDGE,"E12.2")])]});
            var Q26;
            Q26=makeQuery(id+"F1.opExtrude","SWEPT_EDGE",EDGE,{"disambiguationData":[OSD([sQuery(id+"F0.wireOp",EDGE,"E7.0"),sQuery(id+"F0.wireOp",EDGE,"E7.1")])]});
            var Q27;
            Q27=makeQuery(id+"F1.opExtrude","SWEPT_EDGE",EDGE,{"disambiguationData":[OSD([sQuery(id+"F0.wireOp",EDGE,"E8.0"),sQuery(id+"F0.wireOp",EDGE,"E10")])]});
            var Q28;
            Q28=makeQuery(id+"F1.opExtrude","SWEPT_EDGE",EDGE,{"disambiguationData":[OSD([sQuery(id+"F0.wireOp",EDGE,"E7.1"),sQuery(id+"F0.wireOp",EDGE,"E7.2")])]});
            var Q29;
            Q29=makeQuery(id+"F1.opExtrude","SWEPT_EDGE",EDGE,{"disambiguationData":[OSD([sQuery(id+"F0.wireOp",EDGE,"E8.0"),sQuery(id+"F0.wireOp",EDGE,"E8.1")])]});
            var Q30;
            Q30=makeQuery(id+"F1.opExtrude","SWEPT_EDGE",EDGE,{"disambiguationData":[OSD([sQuery(id+"F0.wireOp",EDGE,"E12.0"),sQuery(id+"F0.wireOp",EDGE,"E12.1")])]});
            var Q31;
            Q31=makeQuery(id+"F1.opExtrude","SWEPT_EDGE",EDGE,{"disambiguationData":[OSD([sQuery(id+"F0.wireOp",EDGE,"E3.0"),sQuery(id+"F0.wireOp",EDGE,"E3.3")])]});
            var Q32;
            Q32=makeQuery(id+"F1.opExtrude","SWEPT_EDGE",EDGE,{"disambiguationData":[OSD([sQuery(id+"F0.wireOp",EDGE,"E12.2"),sQuery(id+"F0.wireOp",EDGE,"E12.3")])]});
            var Q33;
            Q33=makeQuery(id+"F1.opExtrude","SWEPT_EDGE",EDGE,{"disambiguationData":[OSD([sQuery(id+"F0.wireOp",EDGE,"E10"),sQuery(id+"F0.wireOp",EDGE,"E11.trimOffspring")])]});
            var Q34;
            Q34=makeQuery(id+"F1.opExtrude","SWEPT_EDGE",EDGE,{"disambiguationData":[OSD([sQuery(id+"F0.wireOp",EDGE,"E7.0"),sQuery(id+"F0.wireOp",EDGE,"E9")])]});
            var Q35;
            Q35=makeQuery(id+"F1.opExtrude","SWEPT_EDGE",EDGE,{"disambiguationData":[OSD([sQuery(id+"F0.wireOp",EDGE,"E8.1"),sQuery(id+"F0.wireOp",EDGE,"E11.trimOffspring")])]});
            var Q36;
            Q36=makeQuery(id+"F1.opExtrude","SWEPT_EDGE",EDGE,{"disambiguationData":[OSD([sQuery(id+"F0.wireOp",EDGE,"E7.2"),sQuery(id+"F0.wireOp",EDGE,"E9")])]});
            var Q37;
            Q37=makeQuery(id+"F1.opExtrude","SWEPT_EDGE",EDGE,{"disambiguationData":[OSD([sQuery(id+"F0.wireOp",EDGE,"E3.0"),sQuery(id+"F0.wireOp",EDGE,"E3.1")])]});
            var Q38;
            Q38=makeQuery(id+"F1.opExtrude","SWEPT_EDGE",EDGE,{"disambiguationData":[OSD([sQuery(id+"F0.wireOp",EDGE,"E12.0"),sQuery(id+"F0.wireOp",EDGE,"E12.3")])]});
            fillet(context, id + "F16", {"entities" : qUnion([Q0, Q1, Q2, Q3, Q4, Q5, Q6, Q7, Q8, Q9, Q10, Q11, Q12, Q13, Q14, Q15, Q16, Q17, Q18, Q19, Q20, Q21, Q22, Q23, Q24, Q25, Q26, Q27, Q28, Q29, Q30, Q31, Q32, Q33, Q34, Q35, Q36, Q37, Q38]), "radius" : 2 * mm, "tangentPropagation" : true, "allowEdgeOverflow" : false});
        }
        {
            var Q0;
            Q0=qCreatedBy(makeId("Top.planeOp"),FACE);
            var sketch = newSketch(context, id + "F17", { "sketchPlane" : qUnion([Q0])});
            skCircle(sketch, "E31.cCircle", {"center": v(14.5, -33.75) * mm, "radius": 6.25 * mm});
            skLineSegment(sketch, "E31.0", {"start": v(20.75, -30.14) * mm, "end": v(20.75, -37.36) * mm, "construction": true});
            skLineSegment(sketch, "E31.1", {"start": v(20.75, -37.36) * mm, "end": v(14.5, -40.97) * mm});
            skLineSegment(sketch, "E31.2", {"start": v(14.5, -40.97) * mm, "end": v(8.25, -37.36) * mm});
            skLineSegment(sketch, "E31.3", {"start": v(8.25, -37.36) * mm, "end": v(8.25, -30.14) * mm});
            skLineSegment(sketch, "E31.4", {"start": v(8.25, -30.14) * mm, "end": v(14.5, -26.53) * mm});
            skLineSegment(sketch, "E31.5", {"start": v(14.5, -26.53) * mm, "end": v(20.75, -30.14) * mm, "construction": true});
            skPoint(sketch, "E31.0.midPoint", {"position": v(20.75, -33.75) * mm});
            skLineSegment(sketch, "E32.1.0", {"start": v(40.97, 14.5) * mm, "end": v(37.36, 8.25) * mm});
            skLineSegment(sketch, "E32.1.1", {"start": v(37.36, 20.75) * mm, "end": v(40.97, 14.5) * mm});
            skLineSegment(sketch, "E32.1.2", {"start": v(30.14, 20.75) * mm, "end": v(37.36, 20.75) * mm});
            skLineSegment(sketch, "E32.1.3", {"start": v(26.53, 14.5) * mm, "end": v(30.14, 20.75) * mm});
            skLineSegment(sketch, "E32.1.4", {"start": v(30.14, 8.25) * mm, "end": v(26.53, 14.5) * mm});
            skLineSegment(sketch, "E32.1.5", {"start": v(37.36, 8.25) * mm, "end": v(30.14, 8.25) * mm});
            skLineSegment(sketch, "E32.2.0", {"start": v(-14.5, 40.97) * mm, "end": v(-8.25, 37.36) * mm});
            skLineSegment(sketch, "E32.2.1", {"start": v(-20.75, 37.36) * mm, "end": v(-14.5, 40.97) * mm});
            skLineSegment(sketch, "E32.2.2", {"start": v(-20.75, 30.14) * mm, "end": v(-20.75, 37.36) * mm});
            skLineSegment(sketch, "E32.2.3", {"start": v(-14.5, 26.53) * mm, "end": v(-20.75, 30.14) * mm});
            skLineSegment(sketch, "E32.2.4", {"start": v(-8.25, 30.14) * mm, "end": v(-14.5, 26.53) * mm});
            skLineSegment(sketch, "E32.2.5", {"start": v(-8.25, 37.36) * mm, "end": v(-8.25, 30.14) * mm});
            skLineSegment(sketch, "E32.3.0", {"start": v(-40.97, -14.5) * mm, "end": v(-37.36, -8.25) * mm});
            skLineSegment(sketch, "E32.3.1", {"start": v(-37.36, -20.75) * mm, "end": v(-40.97, -14.5) * mm});
            skLineSegment(sketch, "E32.3.2", {"start": v(-30.14, -20.75) * mm, "end": v(-37.36, -20.75) * mm});
            skLineSegment(sketch, "E32.3.3", {"start": v(-26.53, -14.5) * mm, "end": v(-30.14, -20.75) * mm});
            skLineSegment(sketch, "E32.3.4", {"start": v(-30.14, -8.25) * mm, "end": v(-26.53, -14.5) * mm});
            skLineSegment(sketch, "E32.3.5", {"start": v(-37.36, -8.25) * mm, "end": v(-30.14, -8.25) * mm});
            skPoint(sketch, "E32.center", {"position": v(0, 0) * mm});
            skCircle(sketch, "E33.cCircle", {"center": v(0, 0) * mm, "radius": 5.75 * mm});
            skLineSegment(sketch, "E33.0", {"start": v(3.32, -5.75) * mm, "end": v(-3.32, -5.75) * mm});
            skLineSegment(sketch, "E33.1", {"start": v(-3.32, -5.75) * mm, "end": v(-6.64, 0) * mm});
            skLineSegment(sketch, "E33.2", {"start": v(-6.64, 0) * mm, "end": v(-3.32, 5.75) * mm});
            skLineSegment(sketch, "E33.3", {"start": v(-3.32, 5.75) * mm, "end": v(3.32, 5.75) * mm});
            skLineSegment(sketch, "E33.4", {"start": v(3.32, 5.75) * mm, "end": v(6.64, 0) * mm});
            skLineSegment(sketch, "E33.5", {"start": v(6.64, 0) * mm, "end": v(3.32, -5.75) * mm});
            skPoint(sketch, "E33.0.midPoint", {"position": v(0, -5.75) * mm});
            skLineSegment(sketch, "E34.bottom", {"start": v(20, -21) * mm, "end": v(9, -21) * mm, "construction": true});
            skLineSegment(sketch, "E34.top", {"start": v(20, -46.5) * mm, "end": v(9, -46.5) * mm, "construction": true});
            skLineSegment(sketch, "E34.left", {"start": v(20, -21) * mm, "end": v(20, -46.5) * mm, "construction": true});
            skLineSegment(sketch, "E34.right", {"start": v(9, -21) * mm, "end": v(9, -46.5) * mm, "construction": true});
            skLineSegment(sketch, "E35.1.0", {"start": v(46.5, 20) * mm, "end": v(46.5, 9) * mm, "construction": true});
            skLineSegment(sketch, "E35.1.1", {"start": v(21, 9) * mm, "end": v(46.5, 9) * mm, "construction": true});
            skLineSegment(sketch, "E35.1.2", {"start": v(21, 20) * mm, "end": v(46.5, 20) * mm, "construction": true});
            skLineSegment(sketch, "E35.1.3", {"start": v(21, 20) * mm, "end": v(21, 9) * mm, "construction": true});
            skLineSegment(sketch, "E35.2.0", {"start": v(-20, 46.5) * mm, "end": v(-9, 46.5) * mm, "construction": true});
            skLineSegment(sketch, "E35.2.1", {"start": v(-9, 21) * mm, "end": v(-9, 46.5) * mm, "construction": true});
            skLineSegment(sketch, "E35.2.2", {"start": v(-20, 21) * mm, "end": v(-20, 46.5) * mm, "construction": true});
            skLineSegment(sketch, "E35.2.3", {"start": v(-20, 21) * mm, "end": v(-9, 21) * mm, "construction": true});
            skLineSegment(sketch, "E35.3.0", {"start": v(-46.5, -20) * mm, "end": v(-46.5, -9) * mm, "construction": true});
            skLineSegment(sketch, "E35.3.1", {"start": v(-21, -9) * mm, "end": v(-46.5, -9) * mm, "construction": true});
            skLineSegment(sketch, "E35.3.2", {"start": v(-21, -20) * mm, "end": v(-46.5, -20) * mm, "construction": true});
            skLineSegment(sketch, "E35.3.3", {"start": v(-21, -20) * mm, "end": v(-21, -9) * mm, "construction": true});
            skSolve(sketch);
        }
        {
            var Q0;
            Q0 = qSketchRegion(id + "F17", true);
            extrude(context, id + "F18", {"entities" : qUnion([Q0]), "operationType" : NewBodyOperationType.REMOVE, "depth" : 4 * mm, "offsetDistance" : 25 * mm});
        }
        {
            var Q0;
            {var subQ0=sQuery(id+"F0.wireOp",EDGE,"E12.0");var subQ1=sQuery(id+"F0.wireOp",EDGE,"E12.1");var subQ2=sQuery(id+"F0.wireOp",EDGE,"E12.2");var subQ3=sQuery(id+"F0.wireOp",EDGE,"E12.3");var subQ4=sQuery(id+"F0.wireOp",EDGE,"E18");var subQ5=sQuery(id+"F0.wireOp",EDGE,"E17");var subQ6=sQuery(id+"F0.wireOp",EDGE,"E16");var subQ7=sQuery(id+"F0.wireOp",EDGE,"E15");var subQ8=sQuery(id+"F0.wireOp",EDGE,"E6.right");var subQ9=sQuery(id+"F0.wireOp",EDGE,"E6.bottom");var subQ10=sQuery(id+"F0.wireOp",EDGE,"E5.left");var subQ11=sQuery(id+"F0.wireOp",EDGE,"E5.top");var subQ12=sQuery(id+"F0.wireOp",EDGE,"E4.right");var subQ13=sQuery(id+"F0.wireOp",EDGE,"E4.bottom");var subQ14=sQuery(id+"F0.wireOp",EDGE,"E2.right");var subQ15=sQuery(id+"F0.wireOp",EDGE,"E2.top");var subQ16=sQuery(id+"F0.wireOp",EDGE,"E1");var subQ17=makeQuery(id+"F2.opExtrude","CAP_FACE",FACE,{"disambiguationData":[OSD([subQ16,subQ15,subQ14,subQ13,subQ12,subQ11,subQ10,subQ9,subQ8,subQ7,subQ6,subQ5,subQ4])],"isStart":false});var subQ18=sQuery(id+"F0.wireOp",EDGE,"E8.0");var subQ19=sQuery(id+"F0.wireOp",EDGE,"E8.1");var subQ20=sQuery(id+"F0.wireOp",EDGE,"E10");var subQ21=sQuery(id+"F0.wireOp",EDGE,"E11.trimOffspring");var subQ22=sQuery(id+"F0.wireOp",EDGE,"E7.0");var subQ23=sQuery(id+"F0.wireOp",EDGE,"E9");var subQ24=sQuery(id+"F0.wireOp",EDGE,"E7.1");var subQ25=sQuery(id+"F0.wireOp",EDGE,"E7.2");var subQ26=sQuery(id+"F0.wireOp",EDGE,"E3.0");var subQ27=sQuery(id+"F0.wireOp",EDGE,"E3.1");var subQ28=sQuery(id+"F0.wireOp",EDGE,"E3.2");var subQ29=sQuery(id+"F0.wireOp",EDGE,"E3.3");Q0=makeQuery(id+"F4.boolean.opBoolean","MERGE",FACE,{"derivedFrom":[makeQuery(id+"F3.opExtrude","CAP_FACE",FACE,{"disambiguationData":[OSD([subQ16,subQ15,subQ14,subQ26,subQ27,subQ28,subQ29,subQ13,subQ12,subQ11,subQ10,subQ9,subQ8,subQ22,subQ24,subQ25,subQ18,subQ19,subQ23,subQ20,subQ21,subQ0,subQ1,subQ2,subQ3,subQ7,subQ6,subQ5,subQ4])],"isStart":false}),makeQuery(id+"F4.opExtrude","CAP_FACE",FACE,{"disambiguationData":[OSD([subQ16,subQ15,subQ14,subQ13,subQ12,subQ11,subQ10,subQ9,subQ8,subQ7,subQ6,subQ5,subQ4]),TDD([makeQuery(id+"F2.boolean.opBoolean","SPLIT",FACE,{"disambiguationData":[TD([makeQuery(id+"F1.opExtrude","SWEPT_FACE",FACE,{"disambiguationData":[OSD([subQ26])]})])],"derivedFrom":subQ17})])],"isStart":false}),makeQuery(id+"F4.opExtrude","CAP_FACE",FACE,{"disambiguationData":[OSD([subQ16,subQ15,subQ14,subQ13,subQ12,subQ11,subQ10,subQ9,subQ8,subQ7,subQ6,subQ5,subQ4]),TDD([makeQuery(id+"F2.boolean.opBoolean","SPLIT",FACE,{"disambiguationData":[TD([makeQuery(id+"F1.opExtrude","SWEPT_FACE",FACE,{"disambiguationData":[OSD([subQ22])]})])],"derivedFrom":subQ17})])],"isStart":false}),makeQuery(id+"F4.opExtrude","CAP_FACE",FACE,{"disambiguationData":[OSD([subQ16,subQ15,subQ14,subQ13,subQ12,subQ11,subQ10,subQ9,subQ8,subQ7,subQ6,subQ5,subQ4]),TDD([makeQuery(id+"F2.boolean.opBoolean","SPLIT",FACE,{"disambiguationData":[TD([makeQuery(id+"F1.opExtrude","SWEPT_FACE",FACE,{"disambiguationData":[OSD([subQ18])]})])],"derivedFrom":subQ17})])],"isStart":false}),makeQuery(id+"F4.opExtrude","CAP_FACE",FACE,{"disambiguationData":[OSD([subQ16,subQ15,subQ14,subQ13,subQ12,subQ11,subQ10,subQ9,subQ8,subQ7,subQ6,subQ5,subQ4]),TDD([makeQuery(id+"F2.boolean.opBoolean","SPLIT",FACE,{"disambiguationData":[TD([makeQuery(id+"F1.opExtrude","SWEPT_FACE",FACE,{"disambiguationData":[OSD([subQ0])]})])],"derivedFrom":subQ17})])],"isStart":false})]});}
            var sketch = newSketch(context, id + "F19", { "sketchPlane" : qUnion([Q0])});
            skCircle(sketch, "E36", {"center": v(-14.5, 33.75) * mm, "radius": 6.5 * mm});
            skCircle(sketch, "E37.1.0", {"center": v(-33.75, -14.5) * mm, "radius": 6.5 * mm});
            skCircle(sketch, "E37.2.0", {"center": v(14.5, -33.75) * mm, "radius": 6.5 * mm});
            skCircle(sketch, "E37.3.0", {"center": v(33.75, 14.5) * mm, "radius": 6.5 * mm});
            skPoint(sketch, "E37.center", {"position": v(0, 0) * mm});
            skCircle(sketch, "E38", {"center": v(0, 0) * mm, "radius": 6.5 * mm});
            skSolve(sketch);
        }
        {
            var Q0;
            Q0 = qSketchRegion(id + "F19", true);
            extrude(context, id + "F20", {"entities" : qUnion([Q0]), "operationType" : NewBodyOperationType.REMOVE, "oppositeDirection" : true, "depth" : 8 * mm, "offsetDistance" : 25 * mm});
        }
    });
